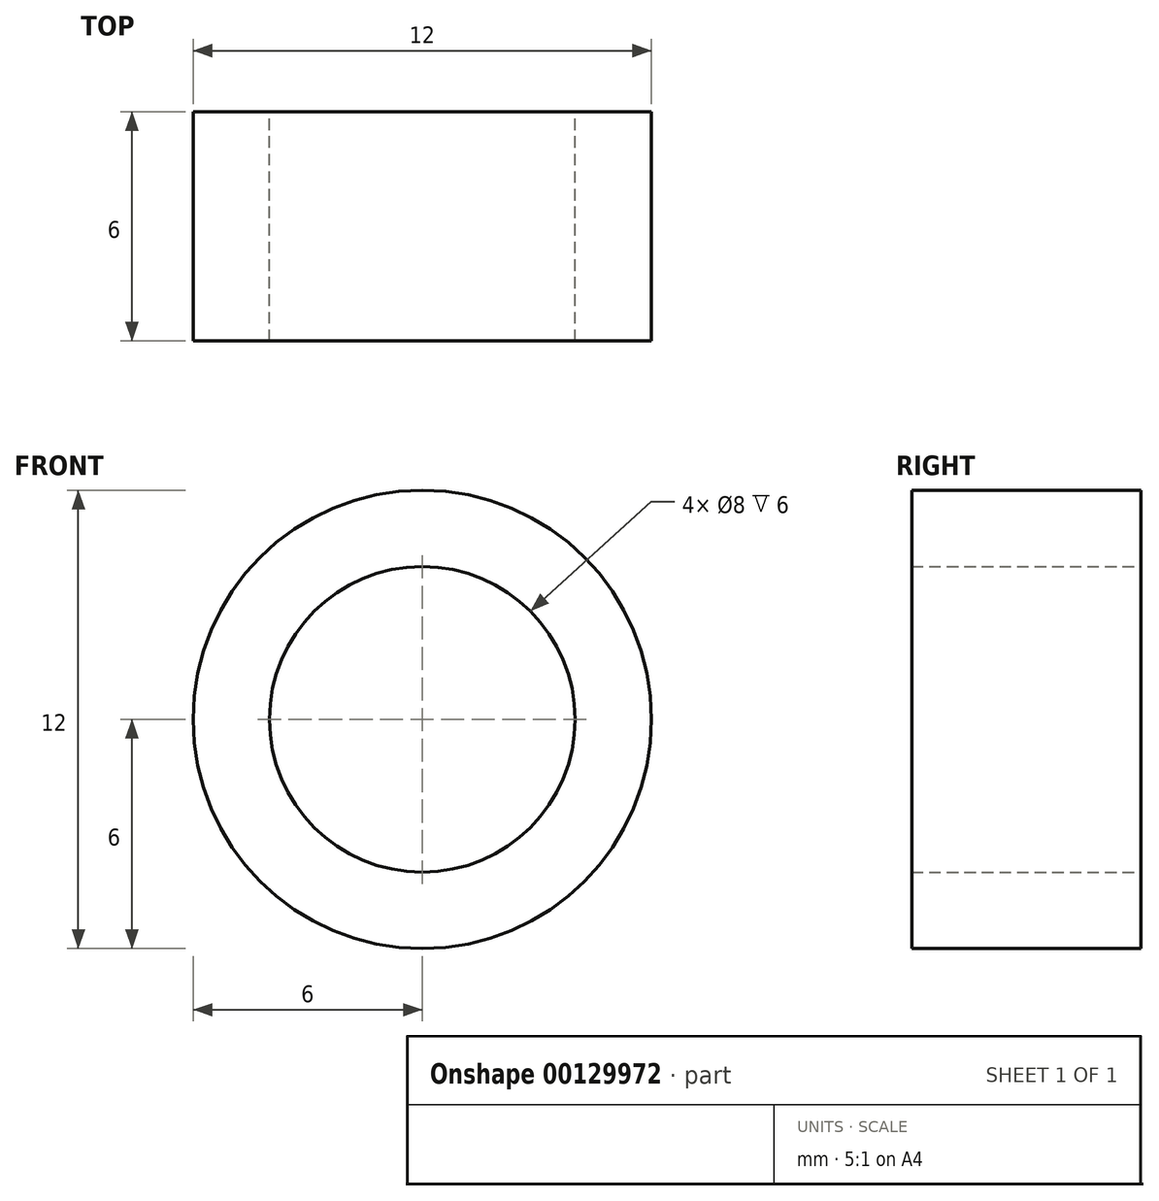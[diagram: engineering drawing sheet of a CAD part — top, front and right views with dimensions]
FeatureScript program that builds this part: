
annotation { "Feature Type Name" : "Feature", "Feature Type Description" : "" }
export const myFeature = defineFeature(function(context is Context, id is Id, definition is map)
    precondition{}
    {
        {
            var Q0;
            Q0=qCreatedBy(makeId("Front.planeOp"),FACE);
            var sketch = newSketch(context, id + "F0", { "sketchPlane" : qUnion([Q0])});
            skCircle(sketch, "E0", {"center": v(0, 0) * mm, "radius": 4 * mm});
            skCircle(sketch, "E1", {"center": v(0, 0) * mm, "radius": 6 * mm});
            skSolve(sketch);
        }
        {
            var Q0;
            Q0=makeQuery(id+"F0.imprint","IMPRINT",FACE,{"disambiguationData":[TD([[makeQuery(id+"F0.imprint","IMPRINT",EDGE,{"derivedFrom":sQuery(id+"F0.wireOp",EDGE,"E0")}),-1.0]])]});
            extrude(context, id + "F1", {"entities" : qUnion([Q0]), "depth" : 6 * mm});
        }
    });
